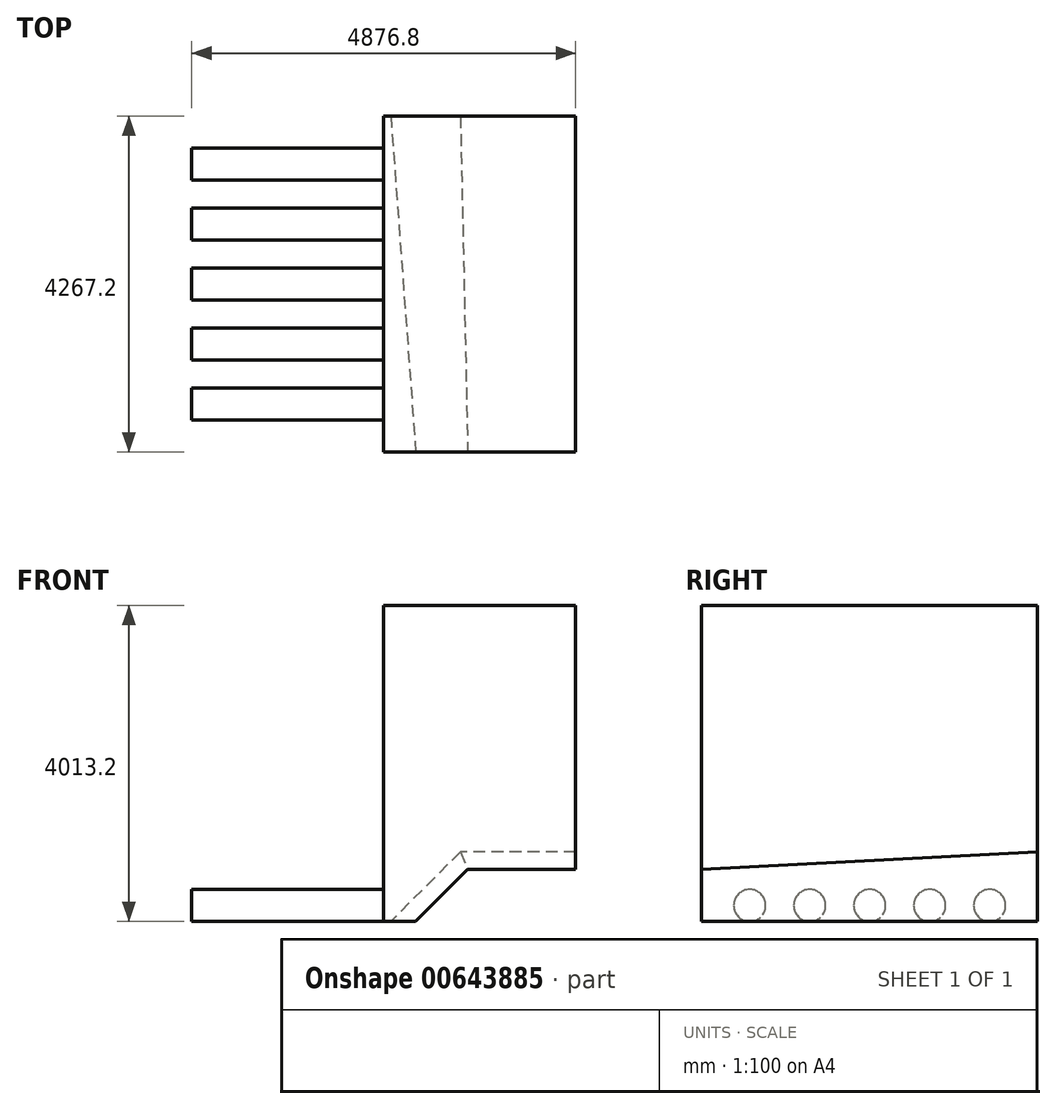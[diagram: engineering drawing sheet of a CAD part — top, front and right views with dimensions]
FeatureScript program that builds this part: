
annotation { "Feature Type Name" : "Feature", "Feature Type Description" : "" }
export const myFeature = defineFeature(function(context is Context, id is Id, definition is map)
    precondition{}
    {
        {
            var Q0;
            Q0=qCreatedBy(makeId("Top.planeOp"),FACE);
            var sketch = newSketch(context, id + "F0", { "sketchPlane" : qUnion([Q0])});
            skLineSegment(sketch, "E0.bottom", {"start": v(0, 0) * mm, "end": v(2438.4, 0) * mm});
            skLineSegment(sketch, "E0.top", {"start": v(0, 4267.2) * mm, "end": v(2438.4, 4267.2) * mm});
            skLineSegment(sketch, "E0.left", {"start": v(0, 0) * mm, "end": v(0, 4267.2) * mm});
            skLineSegment(sketch, "E0.right", {"start": v(2438.4, 0) * mm, "end": v(2438.4, 4267.2) * mm});
            skSolve(sketch);
        }
        {
            var Q0;
            Q0 = qSketchRegion(id + "F0", true);
            extrude(context, id + "F1", {"entities" : qUnion([Q0]), "depth" : 4013.2 * mm, "offsetDistance" : 25.4 * mm});
        }
        {
            var Q0;
            Q0=makeQuery(id+"F1.opExtrude","SWEPT_FACE",FACE,{"disambiguationData":[OSD([sQuery(id+"F0.wireOp",EDGE,"E0.bottom")])]});
            var sketch = newSketch(context, id + "F2", { "sketchPlane" : qUnion([Q0])});
            skLineSegment(sketch, "E1", {"start": v(2438.4, 0) * mm, "end": v(2438.4, 660.4) * mm});
            skLineSegment(sketch, "E2", {"start": v(2438.4, 0) * mm, "end": v(406.4, 0) * mm});
            skLineSegment(sketch, "E3", {"start": v(2438.4, 660.4) * mm, "end": v(1066.63, 660.4) * mm});
            skLineSegment(sketch, "E4", {"start": v(1066.63, 660.4) * mm, "end": v(406.4, 0) * mm});
            skSolve(sketch);
        }
        {
            var Q0;
            Q0 = qSketchRegion(id + "F2", true);
            extrude(context, id + "F3", {"entities" : qUnion([Q0]), "operationType" : NewBodyOperationType.REMOVE, "oppositeDirection" : true, "depth" : 4267.2 * mm, "offsetDistance" : 25.4 * mm, "hasDraft" : true, "draftAngle" : 3 * degree});
        }
        {
            var Q0;
            Q0=makeQuery(id+"F1.opExtrude","SWEPT_FACE",FACE,{"disambiguationData":[OSD([sQuery(id+"F0.wireOp",EDGE,"E0.left")])]});
            var sketch = newSketch(context, id + "F4", { "sketchPlane" : qUnion([Q0])});
            skLineSegment(sketch, "E5", {"start": v(-4267.2, 0) * mm, "end": v(-3657.6, 0) * mm});
            skLineSegment(sketch, "E6", {"start": v(-3657.6, 0) * mm, "end": v(-2895.6, 0) * mm});
            skLineSegment(sketch, "E7", {"start": v(-2895.6, 0) * mm, "end": v(-2133.6, 0) * mm});
            skLineSegment(sketch, "E8", {"start": v(-2133.6, 0) * mm, "end": v(-1371.6, 0) * mm});
            skLineSegment(sketch, "E9", {"start": v(-1371.6, 0) * mm, "end": v(-609.6, 0) * mm});
            skLineSegment(sketch, "E10", {"start": v(-609.6, 0) * mm, "end": v(0, 0) * mm});
            skCircle(sketch, "E11", {"center": v(-3657.6, 203.2) * mm, "radius": 203.2 * mm});
            skCircle(sketch, "E12", {"center": v(-2895.6, 203.2) * mm, "radius": 203.2 * mm});
            skCircle(sketch, "E13", {"center": v(-2133.6, 203.2) * mm, "radius": 203.2 * mm});
            skCircle(sketch, "E14", {"center": v(-1371.6, 203.2) * mm, "radius": 203.2 * mm});
            skCircle(sketch, "E15", {"center": v(-609.6, 203.2) * mm, "radius": 203.2 * mm});
            skSolve(sketch);
        }
        {
            var Q0;
            Q0 = qSketchRegion(id + "F4", true);
            extrude(context, id + "F5", {"entities" : qUnion([Q0]), "operationType" : NewBodyOperationType.ADD, "depth" : 2438.4 * mm, "offsetDistance" : 25.4 * mm});
        }
    });
